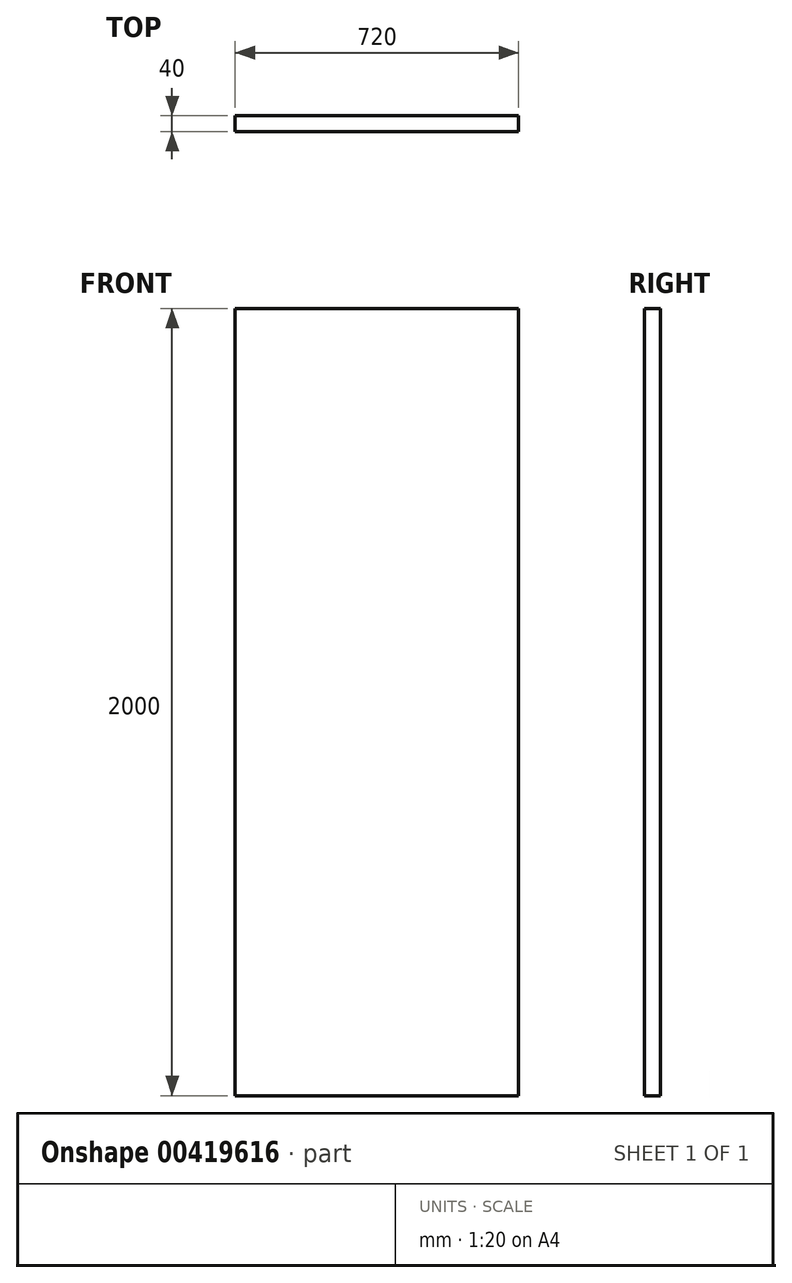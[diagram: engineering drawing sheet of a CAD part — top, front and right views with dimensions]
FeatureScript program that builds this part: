
annotation { "Feature Type Name" : "Feature", "Feature Type Description" : "" }
export const myFeature = defineFeature(function(context is Context, id is Id, definition is map)
    precondition{}
    {
        {
            var Q0;
            Q0=qCreatedBy(makeId("Top.planeOp"),FACE);
            var sketch = newSketch(context, id + "F0", { "sketchPlane" : qUnion([Q0])});
            skLineSegment(sketch, "E0.bottom", {"start": v(-584.7, 30.87) * mm, "end": v(135.3, 30.87) * mm});
            skLineSegment(sketch, "E0.top", {"start": v(-584.7, -9.13) * mm, "end": v(135.3, -9.13) * mm});
            skLineSegment(sketch, "E0.left", {"start": v(-584.7, 30.87) * mm, "end": v(-584.7, -9.13) * mm});
            skLineSegment(sketch, "E0.right", {"start": v(135.3, 30.87) * mm, "end": v(135.3, -9.13) * mm});
            skSolve(sketch);
        }
        {
            var Q0;
            Q0=makeQuery(id+"F0.imprint","IMPRINT",FACE,{"disambiguationData":[TD([[makeQuery(id+"F0.imprint","IMPRINT",EDGE,{"derivedFrom":sQuery(id+"F0.wireOp",EDGE,"E0.bottom")}),-1.0]])]});
            extrude(context, id + "F1", {"entities" : qUnion([Q0]), "depth" : 2000 * mm});
        }
    });
